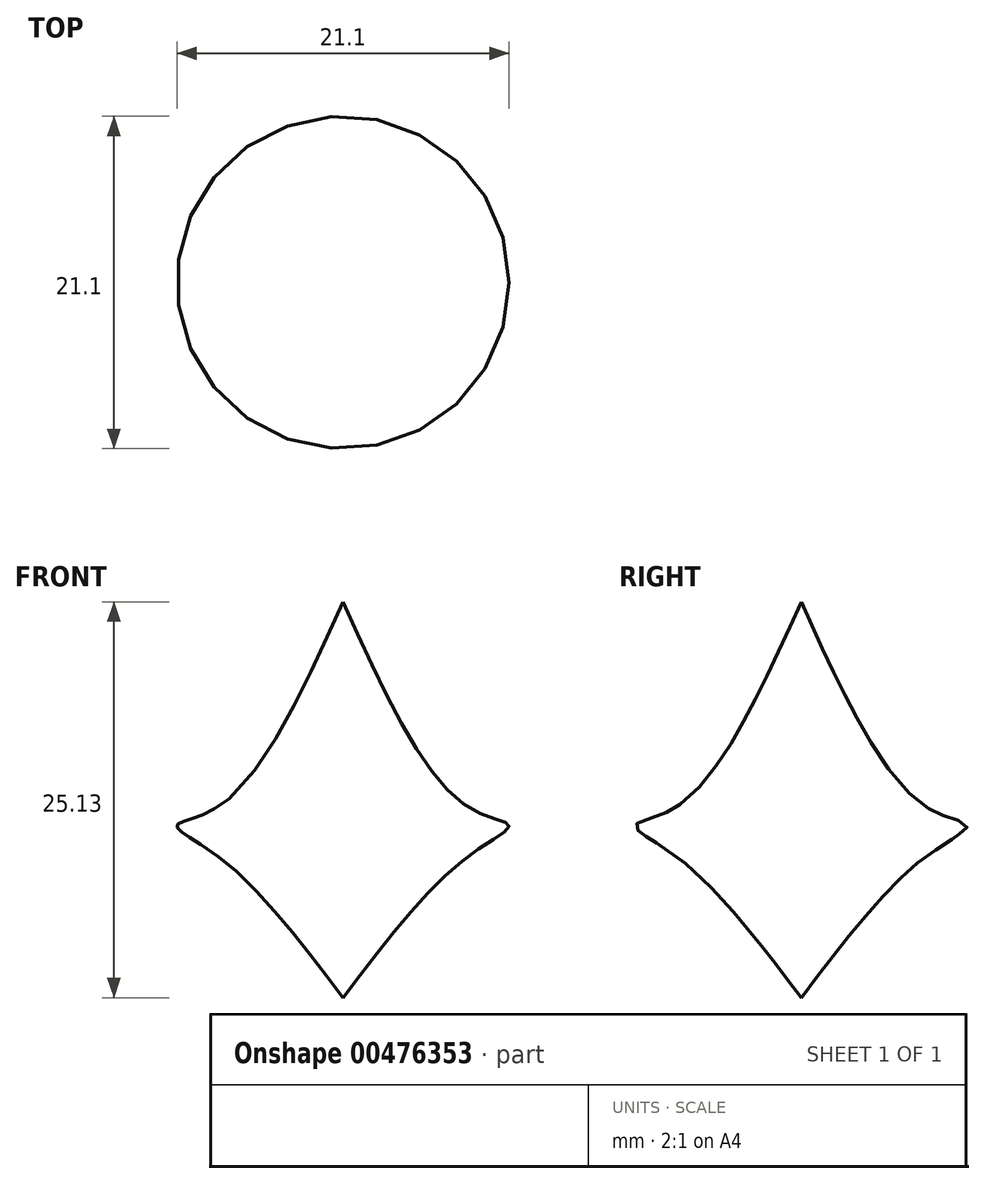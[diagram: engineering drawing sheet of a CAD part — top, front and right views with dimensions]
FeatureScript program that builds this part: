
annotation { "Feature Type Name" : "Feature", "Feature Type Description" : "" }
export const myFeature = defineFeature(function(context is Context, id is Id, definition is map)
    precondition{}
    {
        {
            var Q0;
            Q0=qCreatedBy(makeId("Front.planeOp"),FACE);
            var sketch = newSketch(context, id + "F0", { "sketchPlane" : qUnion([Q0])});
            skFitSpline(sketch, "E0", {"points": [v(0, 25.13) * mm, v(7.92, 12.13) * mm, v(10.55, 10.93) * mm, v(7.84, 8.9) * mm, v(0, 0) * mm], "startDerivative": vector(21.14, -46.75) * mm, "endDerivative": vector(-24.84, -32.84) * mm});
            skLineSegment(sketch, "E1", {"start": v(0, 25.13) * mm, "end": v(0, 0) * mm});
            skSolve(sketch);
        }
        {
            var Q0;
            Q0=sQuery(id+"F0.wireOp",EDGE,"E0");
            var Q1;
            Q1=sQuery(id+"F0.wireOp",EDGE,"E1");
            revolve(context, id + "F1", {"bodyType" : ToolBodyType.SURFACE, "surfaceEntities" : qUnion([Q0]), "axis" : qUnion([Q1]), "revolveType" : RevolveType.FULL});
        }
    });
